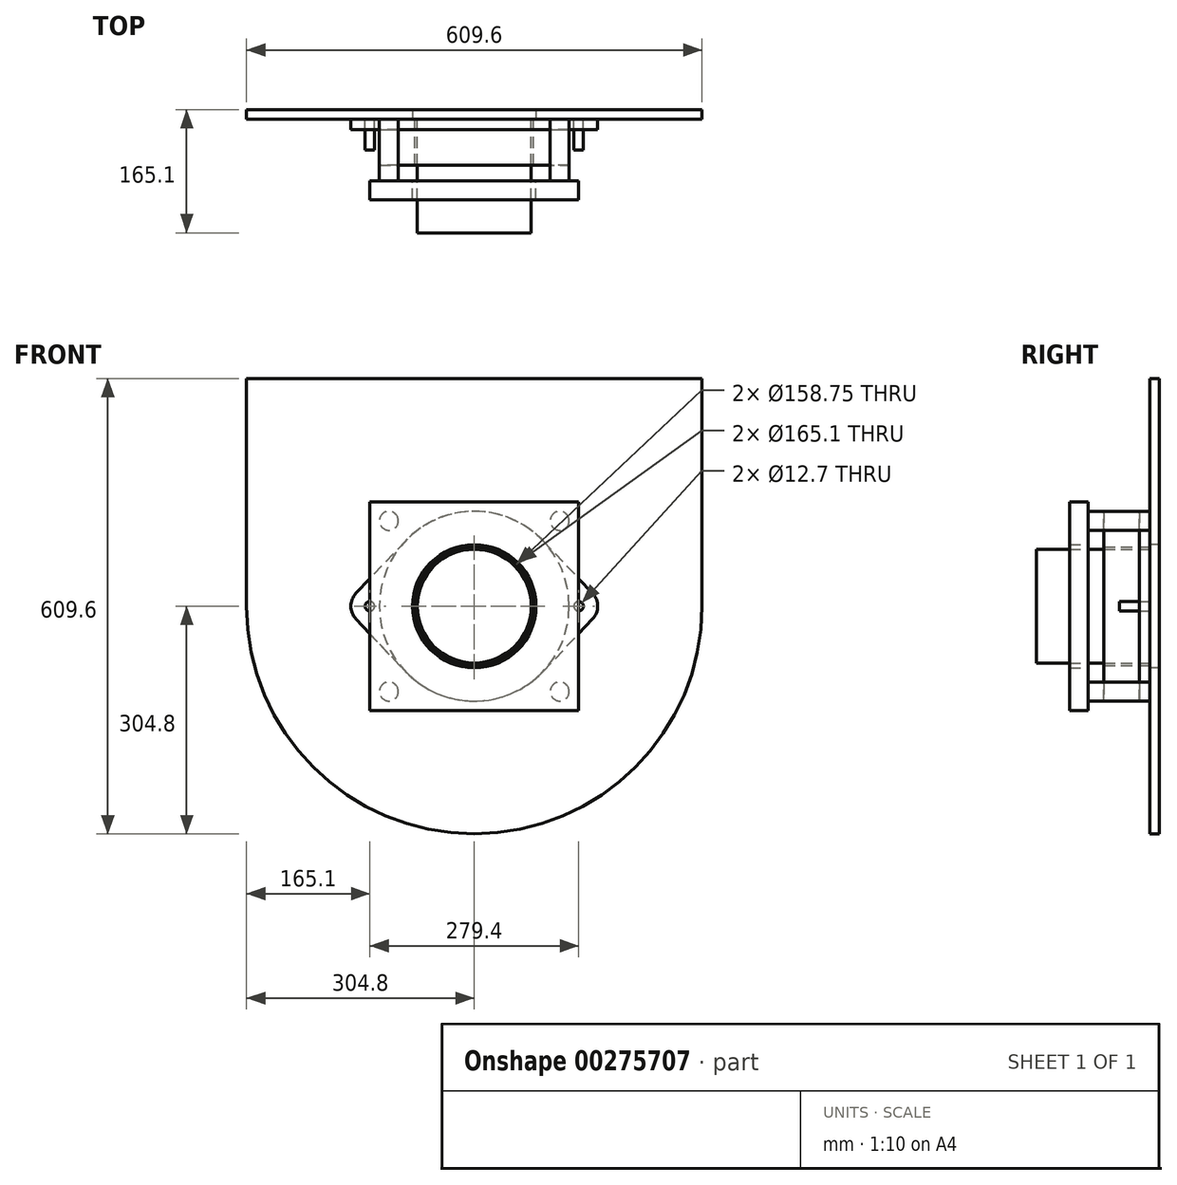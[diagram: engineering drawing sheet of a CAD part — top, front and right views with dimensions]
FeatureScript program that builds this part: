
annotation { "Feature Type Name" : "Feature", "Feature Type Description" : "" }
export const myFeature = defineFeature(function(context is Context, id is Id, definition is map)
    precondition{}
    {
        {
            var Q0;
            Q0=qCreatedBy(makeId("Front.planeOp"),FACE);
            var sketch = newSketch(context, id + "F0", { "sketchPlane" : qUnion([Q0])});
            skCircle(sketch, "E0", {"center": v(0, 0) * mm, "radius": 82.55 * mm});
            skArc(sketch, "E1", {"start": v(-304.8, 0) * mm, "mid": v(0, -304.8) * mm, "end": v(304.8, 0) * mm});
            skLineSegment(sketch, "E2", {"start": v(304.8, 0) * mm, "end": v(304.8, 304.8) * mm});
            skLineSegment(sketch, "E3", {"start": v(304.8, 304.8) * mm, "end": v(-304.8, 304.8) * mm});
            skLineSegment(sketch, "E4", {"start": v(-304.8, 0) * mm, "end": v(-304.8, 304.8) * mm});
            skSolve(sketch);
        }
        {
            var Q0;
            Q0=makeQuery(id+"F0.imprint","IMPRINT",FACE,{"disambiguationData":[TD([[makeQuery(id+"F0.imprint","IMPRINT",EDGE,{"derivedFrom":sQuery(id+"F0.wireOp",EDGE,"E0")}),-1.0]])]});
            extrude(context, id + "F1", {"entities" : qUnion([Q0]), "oppositeDirection" : true, "depth" : 12.7 * mm, "offsetDistance" : 25.4 * mm});
        }
        {
            var Q0;
            Q0=qCreatedBy(makeId("Front.planeOp"),FACE);
            var sketch = newSketch(context, id + "F2", { "sketchPlane" : qUnion([Q0])});
            skCircle(sketch, "E5", {"center": v(0, 0) * mm, "radius": 76.2 * mm});
            skLineSegment(sketch, "E6.bottom", {"start": v(-114.3, 114.3) * mm, "end": v(114.3, 114.3) * mm, "construction": true});
            skLineSegment(sketch, "E6.top", {"start": v(-114.3, -114.3) * mm, "end": v(114.3, -114.3) * mm, "construction": true});
            skLineSegment(sketch, "E6.left", {"start": v(-114.3, 114.3) * mm, "end": v(-114.3, -114.3) * mm, "construction": true});
            skLineSegment(sketch, "E6.right", {"start": v(114.3, 114.3) * mm, "end": v(114.3, -114.3) * mm, "construction": true});
            skCircle(sketch, "E7", {"center": v(-114.3, 114.3) * mm, "radius": 12.7 * mm});
            skCircle(sketch, "E8", {"center": v(114.3, 114.3) * mm, "radius": 12.7 * mm});
            skCircle(sketch, "E9", {"center": v(114.3, -114.3) * mm, "radius": 12.7 * mm});
            skCircle(sketch, "E10", {"center": v(-114.3, -114.3) * mm, "radius": 12.7 * mm});
            skLineSegment(sketch, "E11", {"start": v(-139.7, 0) * mm, "end": v(139.7, 0) * mm, "construction": true});
            skCircle(sketch, "E12", {"center": v(-139.7, 0) * mm, "radius": 6.35 * mm});
            skCircle(sketch, "E13", {"center": v(139.7, 0) * mm, "radius": 6.35 * mm});
            skSolve(sketch);
        }
        {
            var Q0;
            Q0=makeQuery(id+"F2.imprint","IMPRINT",FACE,{"disambiguationData":[TD([[makeQuery(id+"F2.imprint","IMPRINT",EDGE,{"derivedFrom":sQuery(id+"F2.wireOp",EDGE,"E5")}),1.0]])]});
            extrude(context, id + "F3", {"entities" : qUnion([Q0]), "depth" : 152.4 * mm, "offsetDistance" : 25.4 * mm});
        }
        {
            var Q0;
            Q0=makeQuery(id+"F2.imprint","IMPRINT",FACE,{"disambiguationData":[TD([[makeQuery(id+"F2.imprint","IMPRINT",EDGE,{"derivedFrom":sQuery(id+"F2.wireOp",EDGE,"E12")}),1.0]])]});
            var Q1;
            Q1=makeQuery(id+"F2.imprint","IMPRINT",FACE,{"disambiguationData":[TD([[makeQuery(id+"F2.imprint","IMPRINT",EDGE,{"derivedFrom":sQuery(id+"F2.wireOp",EDGE,"E13")}),1.0]])]});
            extrude(context, id + "F4", {"entities" : qUnion([Q0, Q1]), "operationType" : NewBodyOperationType.ADD, "depth" : 41.27 * mm, "offsetDistance" : 25.4 * mm});
        }
        {
            var Q0;
            Q0=makeQuery(id+"F2.imprint","IMPRINT",FACE,{"disambiguationData":[TD([[makeQuery(id+"F2.imprint","IMPRINT",EDGE,{"derivedFrom":sQuery(id+"F2.wireOp",EDGE,"E8")}),1.0]])]});
            extrude(context, id + "F5", {"entities" : qUnion([Q0]), "operationType" : NewBodyOperationType.ADD, "depth" : 82.55 * mm, "offsetDistance" : 25.4 * mm});
        }
        {
            var Q0;
            Q0=makeQuery(id+"F2.imprint","IMPRINT",FACE,{"disambiguationData":[TD([[makeQuery(id+"F2.imprint","IMPRINT",EDGE,{"derivedFrom":sQuery(id+"F2.wireOp",EDGE,"E7")}),1.0]])]});
            var Q1;
            Q1=makeQuery(id+"F2.imprint","IMPRINT",FACE,{"disambiguationData":[TD([[makeQuery(id+"F2.imprint","IMPRINT",EDGE,{"derivedFrom":sQuery(id+"F2.wireOp",EDGE,"E9")}),1.0]])]});
            var Q2;
            Q2=makeQuery(id+"F2.imprint","IMPRINT",FACE,{"disambiguationData":[TD([[makeQuery(id+"F2.imprint","IMPRINT",EDGE,{"derivedFrom":sQuery(id+"F2.wireOp",EDGE,"E10")}),1.0]])]});
            extrude(context, id + "F6", {"entities" : qUnion([Q0, Q1, Q2]), "operationType" : NewBodyOperationType.ADD, "depth" : 82.55 * mm, "offsetDistance" : 25.4 * mm});
        }
        {
            var Q0;
            Q0=makeQuery(id+"F6.opExtrude","CAP_FACE",FACE,{"disambiguationData":[OSD([sQuery(id+"F2.wireOp",EDGE,"E7")])],"isStart":false});
            var sketch = newSketch(context, id + "F7", { "sketchPlane" : qUnion([Q0])});
            skLineSegment(sketch, "E14.bottom", {"start": v(-139.7, 139.7) * mm, "end": v(139.7, 139.7) * mm});
            skLineSegment(sketch, "E14.top", {"start": v(-139.7, -139.7) * mm, "end": v(139.7, -139.7) * mm});
            skLineSegment(sketch, "E14.left", {"start": v(-139.7, 139.7) * mm, "end": v(-139.7, -139.7) * mm});
            skLineSegment(sketch, "E14.right", {"start": v(139.7, 139.7) * mm, "end": v(139.7, -139.7) * mm});
            skCircle(sketch, "E15.0", {"center": v(0, 0) * mm, "radius": 82.55 * mm});
            skSolve(sketch);
        }
        {
            var Q0;
            Q0=makeQuery(id+"F7.imprint","IMPRINT",FACE,{"disambiguationData":[TD([[makeQuery(id+"F7.imprint","IMPRINT",EDGE,{"derivedFrom":sQuery(id+"F7.wireOp",EDGE,"E14.bottom")}),-1.0]])]});
            var Q1;
            Q1=makeQuery(id+"F7.imprint","IMPRINT",FACE,{"disambiguationData":[TD([[makeQuery(id+"F7.imprint","IMPRINT",EDGE,{"derivedFrom":makeQuery(id+"F6.opExtrude","CAP_EDGE",EDGE,{"disambiguationData":[OSD([sQuery(id+"F2.wireOp",EDGE,"E7")])],"isStart":false})}),1.0]])]});
            extrude(context, id + "F8", {"entities" : qUnion([Q0, Q1]), "operationType" : NewBodyOperationType.ADD, "depth" : 25.4 * mm, "offsetDistance" : 25.4 * mm});
        }
        {
            var Q0;
            Q0=makeQuery(id+"F1.opExtrude","CAP_FACE",FACE,{"disambiguationData":[OSD([sQuery(id+"F0.wireOp",EDGE,"E0"),sQuery(id+"F0.wireOp",EDGE,"E1"),sQuery(id+"F0.wireOp",EDGE,"E2"),sQuery(id+"F0.wireOp",EDGE,"E3"),sQuery(id+"F0.wireOp",EDGE,"E4")])],"isStart":true});
            var sketch = newSketch(context, id + "F9", { "sketchPlane" : qUnion([Q0])});
            skCircle(sketch, "E16", {"center": v(0, 0) * mm, "radius": 79.37 * mm});
            skArc(sketch, "E17", {"start": v(-158.17, 17.43) * mm, "mid": v(-165.1, 0) * mm, "end": v(-158.17, -17.43) * mm});
            skArc(sketch, "E18", {"start": v(158.17, -17.43) * mm, "mid": v(165.1, 0) * mm, "end": v(158.17, 17.43) * mm});
            skLineSegment(sketch, "E19", {"start": v(92.36, 87.17) * mm, "end": v(158.17, 17.43) * mm});
            skLineSegment(sketch, "E20", {"start": v(-92.36, 87.17) * mm, "end": v(-158.17, 17.43) * mm});
            skLineSegment(sketch, "E21", {"start": v(-158.17, -17.43) * mm, "end": v(-92.36, -87.17) * mm});
            skLineSegment(sketch, "E22", {"start": v(92.36, -87.17) * mm, "end": v(158.17, -17.43) * mm});
            skArc(sketch, "E23.trimOffspring", {"start": v(-92.36, -87.17) * mm, "mid": v(0, -127) * mm, "end": v(92.36, -87.17) * mm});
            skArc(sketch, "E24.trimOffspring", {"start": v(92.36, 87.17) * mm, "mid": v(0, 127) * mm, "end": v(-92.36, 87.17) * mm});
            skSolve(sketch);
        }
        {
            var Q0;
            Q0=makeQuery(id+"F9.imprint","IMPRINT",FACE,{"disambiguationData":[TD([[makeQuery(id+"F9.imprint","IMPRINT",EDGE,{"derivedFrom":sQuery(id+"F9.wireOp",EDGE,"E17")}),1.0]])]});
            var Q1;
            Q1=makeQuery(id+"F9.imprint","IMPRINT",FACE,{"disambiguationData":[TD([[makeQuery(id+"F9.imprint","IMPRINT",EDGE,{"derivedFrom":sQuery(id+"F9.wireOp",EDGE,"E16")}),-1.0]])]});
            extrude(context, id + "F10", {"entities" : qUnion([Q0, Q1]), "depth" : 14.22 * mm, "offsetDistance" : 25.4 * mm});
        }
        {
            var Q0;
            Q0=makeQuery(id+"F10.opExtrude","CAP_FACE",FACE,{"disambiguationData":[OSD([sQuery(id+"F2.wireOp",EDGE,"E12"),sQuery(id+"F2.wireOp",EDGE,"E13"),sQuery(id+"F9.wireOp",EDGE,"E16"),sQuery(id+"F9.wireOp",EDGE,"E17"),sQuery(id+"F9.wireOp",EDGE,"E18"),sQuery(id+"F9.wireOp",EDGE,"E19"),sQuery(id+"F9.wireOp",EDGE,"E20"),sQuery(id+"F9.wireOp",EDGE,"E21"),sQuery(id+"F9.wireOp",EDGE,"E22"),sQuery(id+"F9.wireOp",EDGE,"E23.trimOffspring"),sQuery(id+"F9.wireOp",EDGE,"E24.trimOffspring")])],"isStart":false});
            cPlane(context, id + "F11", {"entities" : qUnion([Q0]), "cplaneType" : CPlaneType.OFFSET, "offset" : 0 * mm, "width" : 152.4 * mm, "height" : 152.4 * mm});
        }
        {
            var Q0;
            Q0=qCreatedBy(id+"F11.planeOp",FACE);
            var sketch = newSketch(context, id + "F12", { "sketchPlane" : qUnion([Q0])});
            skCircle(sketch, "E25.0", {"center": v(0, 0) * mm, "radius": 79.37 * mm});
            skCircle(sketch, "E26", {"center": v(0, 0) * mm, "radius": 127 * mm});
            skSolve(sketch);
        }
        {
            var Q0;
            Q0=makeQuery(id+"F12.imprint","IMPRINT",FACE,{"disambiguationData":[TD([[makeQuery(id+"F12.imprint","IMPRINT",EDGE,{"derivedFrom":sQuery(id+"F12.wireOp",EDGE,"E25.0")}),-1.0]])]});
            extrude(context, id + "F13", {"entities" : qUnion([Q0]), "depth" : 47.5 * mm, "offsetDistance" : 25.4 * mm});
        }
    });
